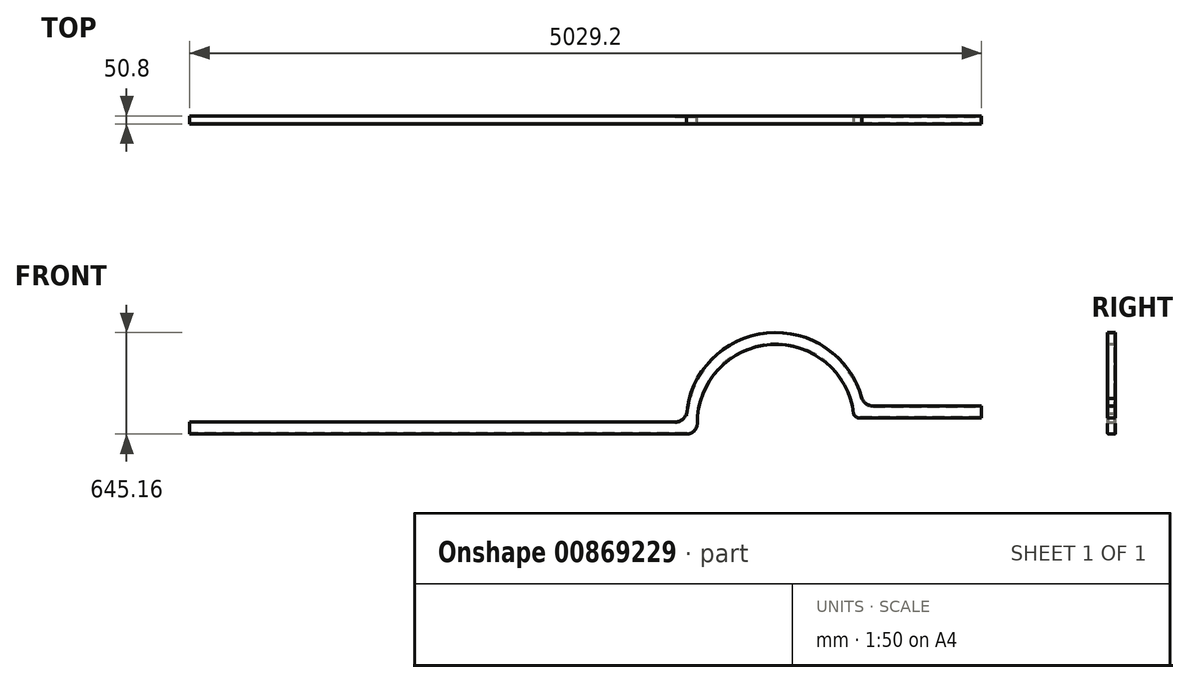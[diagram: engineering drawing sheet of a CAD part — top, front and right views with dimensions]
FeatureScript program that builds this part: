
annotation { "Feature Type Name" : "Feature", "Feature Type Description" : "" }
export const myFeature = defineFeature(function(context is Context, id is Id, definition is map)
    precondition{}
    {
        {
            var Q0;
            Q0=qCreatedBy(makeId("Front.planeOp"),FACE);
            var sketch = newSketch(context, id + "F0", { "sketchPlane" : qUnion([Q0])});
            skLineSegment(sketch, "E0.right", {"start": v(-2514.6, -38.1) * mm, "end": v(-2514.6, 38.1) * mm});
            skPoint(sketch, "E0.middle", {"position": v(0, 0) * mm});
            skPoint(sketch, "E1", {"position": v(-1295.4, 38.1) * mm});
            skPoint(sketch, "E2", {"position": v(1206.5, 38.1) * mm});
            skPoint(sketch, "E3", {"position": v(-1714.5, 38.1) * mm});
            skPoint(sketch, "E4", {"position": v(-1136.14, 38.1) * mm});
            skPoint(sketch, "E5.third.point", {"position": v(1206.5, 607.06) * mm});
            skLineSegment(sketch, "E6.trimOffspring", {"start": v(566.42, 38.1) * mm, "end": v(-2514.6, 38.1) * mm});
            skArc(sketch, "E7", {"start": v(1701.04, 90.42) * mm, "mid": v(1175.51, 529.9) * mm, "end": v(708.66, 28.53) * mm});
            skPoint(sketch, "E7.third.point", {"position": v(1206.5, 530.86) * mm});
            skLineSegment(sketch, "E8.trimOffspring", {"start": v(642.62, -38.1) * mm, "end": v(-2514.6, -38.1) * mm});
            skArc(sketch, "E9", {"start": v(566.42, 38.1) * mm, "mid": v(613.69, 54.53) * mm, "end": v(640.57, 96.75) * mm});
            skArc(sketch, "E10", {"start": v(642.62, -38.1) * mm, "mid": v(689.53, -18.55) * mm, "end": v(708.66, 28.53) * mm});
            skArc(sketch, "E11", {"start": v(1755.37, 187.94) * mm, "mid": v(1783.39, 152.9) * mm, "end": v(1826.26, 139.7) * mm});
            skLineSegment(sketch, "E12", {"start": v(1826.26, 139.7) * mm, "end": v(2514.6, 139.7) * mm});
            skLineSegment(sketch, "E13", {"start": v(2514.6, 139.7) * mm, "end": v(2514.6, 63.5) * mm});
            skLineSegment(sketch, "E14", {"start": v(2514.6, 63.5) * mm, "end": v(1737.46, 63.5) * mm});
            skArc(sketch, "E15.trimOffspring", {"start": v(1755.37, 187.94) * mm, "mid": v(1160.11, 605.17) * mm, "end": v(640.57, 96.75) * mm});
            skArc(sketch, "E16", {"start": v(1701.04, 90.42) * mm, "mid": v(1714.82, 70.96) * mm, "end": v(1737.46, 63.5) * mm});
            skSolve(sketch);
        }
        {
            var Q0;
            Q0 = qSketchRegion(id + "F0", true);
            extrude(context, id + "F1", {"entities" : qUnion([Q0]), "depth" : 50.8 * mm, "offsetDistance" : 25.4 * mm});
        }
        {
            var Q0;
            Q0=makeQuery(id+"F1.opExtrude","SWEPT_FACE",FACE,{"disambiguationData":[OSD([sQuery(id+"F0.wireOp",EDGE,"E0.left")])]});
            var Q1;
            Q1=makeQuery(id+"F1.opExtrude","SWEPT_FACE",FACE,{"disambiguationData":[OSD([sQuery(id+"F0.wireOp",EDGE,"E0.right")])]});
            var Q2;
            Q2=makeQuery(id+"F1.opExtrude","SWEPT_BODY",BODY,{"disambiguationData":[OSD([sQuery(id+"F0.wireOp",EDGE,"E0.bottom"),sQuery(id+"F0.wireOp",EDGE,"E0.top"),sQuery(id+"F0.wireOp",EDGE,"E0.left"),sQuery(id+"F0.wireOp",EDGE,"E0.right")])]});
            shell(context, id + "F2", {"entities" : qUnion([Q0, Q1]), "parts" : qUnion([Q2]), "thickness" : 6.35 * mm});
        }
        {
            var Q0;
            Q0=makeQuery(id+"F1.opExtrude","CAP_EDGE",EDGE,{"disambiguationData":[OSD([sQuery(id+"F0.wireOp",EDGE,"E0.bottom")])],"isStart":true});
            var Q1;
            Q1=makeQuery(id+"F1.opExtrude","CAP_EDGE",EDGE,{"disambiguationData":[OSD([sQuery(id+"F0.wireOp",EDGE,"E0.bottom")])],"isStart":false});
            var Q2;
            Q2=makeQuery(id+"F1.opExtrude","CAP_EDGE",EDGE,{"disambiguationData":[OSD([sQuery(id+"F0.wireOp",EDGE,"E0.top")])],"isStart":false});
            var Q3;
            Q3=makeQuery(id+"F1.opExtrude","CAP_EDGE",EDGE,{"disambiguationData":[OSD([sQuery(id+"F0.wireOp",EDGE,"E0.top")])],"isStart":true});
            var Q4;
            Q4=makeQuery(id+"F1.opExtrude","CAP_EDGE",EDGE,{"disambiguationData":[OSD([sQuery(id+"F0.wireOp",EDGE,"E6.trimOffspring")])],"isStart":false});
            var Q5;
            Q5=makeQuery(id+"F1.opExtrude","CAP_EDGE",EDGE,{"disambiguationData":[OSD([sQuery(id+"F0.wireOp",EDGE,"E6.trimOffspring")])],"isStart":true});
            var Q6;
            Q6=makeQuery(id+"F1.opExtrude","CAP_EDGE",EDGE,{"disambiguationData":[OSD([sQuery(id+"F0.wireOp",EDGE,"E8.trimOffspring")])],"isStart":true});
            var Q7;
            Q7=makeQuery(id+"F1.opExtrude","CAP_EDGE",EDGE,{"disambiguationData":[OSD([sQuery(id+"F0.wireOp",EDGE,"E8.trimOffspring")])],"isStart":false});
            fillet(context, id + "F3", {"entities" : qUnion([Q0, Q1, Q2, Q3, Q4, Q5, Q6, Q7]), "radius" : 5.08 * mm, "tangentPropagation" : true, "allowEdgeOverflow" : false});
        }
    });
